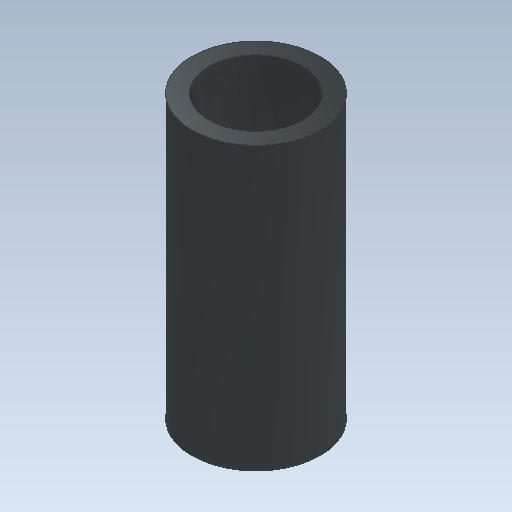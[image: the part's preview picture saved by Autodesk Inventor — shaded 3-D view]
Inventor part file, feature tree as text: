
AUTODESK INVENTOR PART (.ipt)
format: ipt  version: 2020.3 (Build 243373000, 373)  size: 97,280 bytes
history: native  units: mm
features: extrude x1, sketch x1
ambient origin geometry x8: Origin, YZ Plane, XZ Plane, XY Plane, X Axis, Y Axis, Z Axis, Center Point
bodies: Solid1 (feature_tree)
feature tree (2):
  extrude  "Extrusion1"  Depth=10.0mm
  sketch  "Sketch1"  dims[d0=13.6mm d1=10.0mm d2=30.0mm d3=0.0mm]
